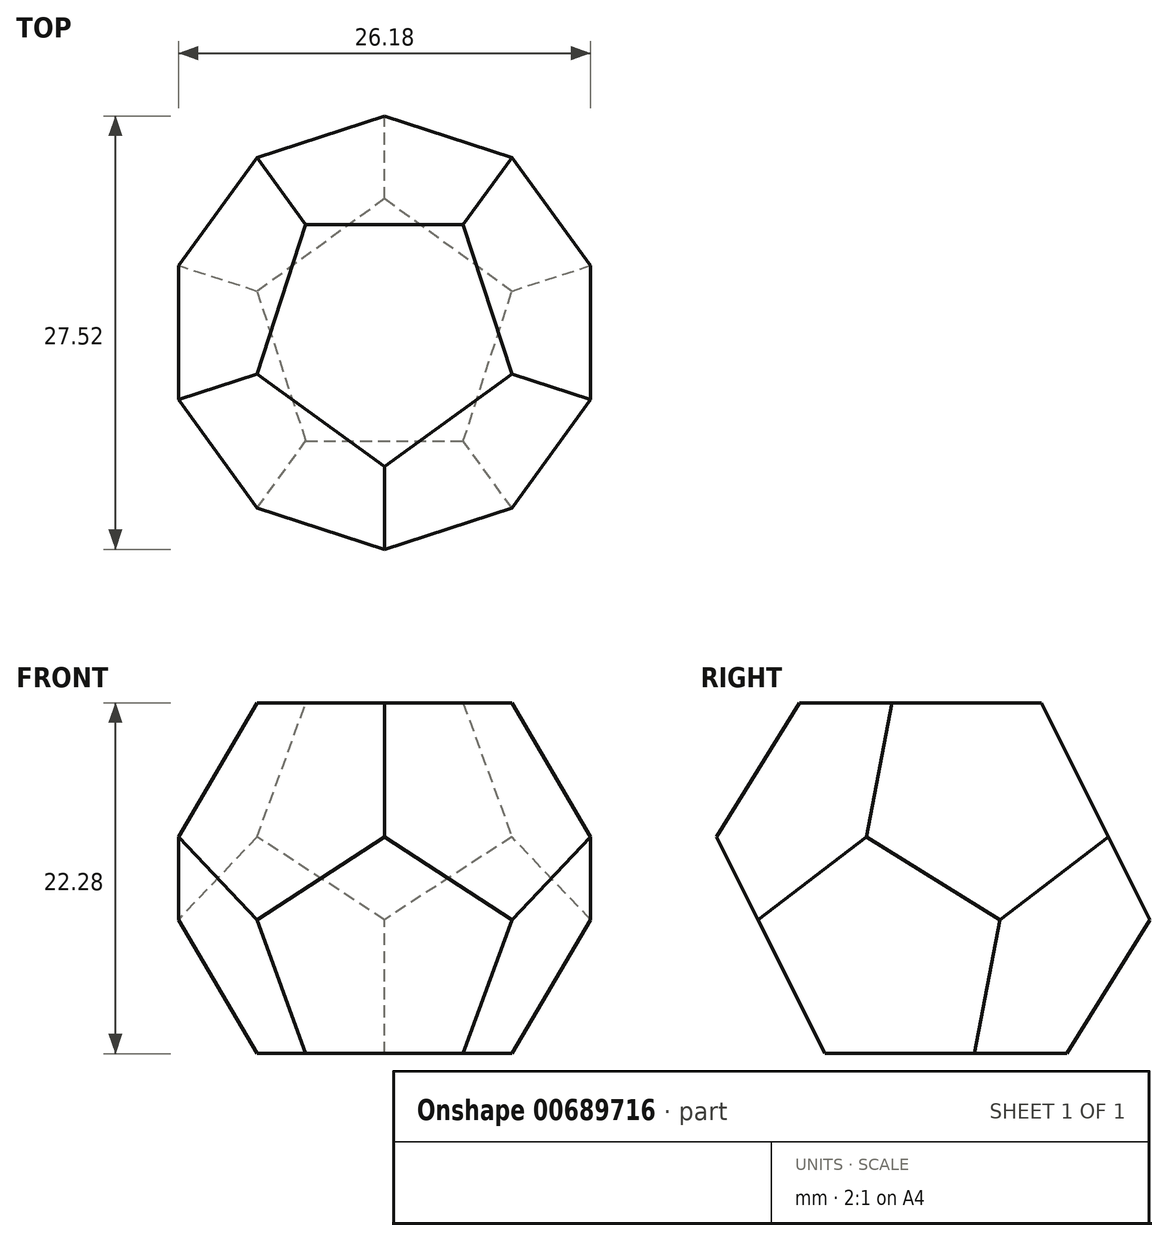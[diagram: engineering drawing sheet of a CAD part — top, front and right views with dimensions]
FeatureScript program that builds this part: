
annotation { "Feature Type Name" : "Feature", "Feature Type Description" : "" }
export const myFeature = defineFeature(function(context is Context, id is Id, definition is map)
    precondition{}
    {
        {
            var Q0;
            Q0=qCreatedBy(makeId("Top.planeOp"),FACE);
            var sketch = newSketch(context, id + "F0", { "sketchPlane" : qUnion([Q0])});
            skCircle(sketch, "E0.cCircle", {"center": v(0, 0) * mm, "radius": 6.88 * mm, "construction": true});
            skLineSegment(sketch, "E0.0", {"start": v(-5, 6.88) * mm, "end": v(5, 6.88) * mm});
            skLineSegment(sketch, "E0.1", {"start": v(5, 6.88) * mm, "end": v(8.1, -2.63) * mm});
            skLineSegment(sketch, "E0.2", {"start": v(8.1, -2.63) * mm, "end": v(0, -8.5) * mm});
            skLineSegment(sketch, "E0.3", {"start": v(0, -8.5) * mm, "end": v(-8.1, -2.63) * mm});
            skLineSegment(sketch, "E0.4", {"start": v(-8.1, -2.63) * mm, "end": v(-5, 6.88) * mm});
            skPoint(sketch, "E0.0.midPoint", {"position": v(0, 6.88) * mm});
            skLineSegment(sketch, "E1", {"start": v(8.1, -2.63) * mm, "end": v(13.1, -4.25) * mm});
            skLineSegment(sketch, "E2", {"start": v(0, -8.5) * mm, "end": v(0, -13.76) * mm});
            skLineSegment(sketch, "E3", {"start": v(-8.1, -2.63) * mm, "end": v(-13.1, -4.25) * mm});
            skLineSegment(sketch, "E4", {"start": v(-5, 6.88) * mm, "end": v(-8.1, 11.14) * mm});
            skLineSegment(sketch, "E5", {"start": v(5, 6.88) * mm, "end": v(8.1, 11.14) * mm});
            skLineSegment(sketch, "E6", {"start": v(0, -13.76) * mm, "end": v(-8.1, -11.14) * mm});
            skLineSegment(sketch, "E7", {"start": v(-8.1, -11.14) * mm, "end": v(-13.1, -4.25) * mm});
            skLineSegment(sketch, "E8", {"start": v(-13.1, -4.25) * mm, "end": v(-13.1, 4.25) * mm});
            skLineSegment(sketch, "E9", {"start": v(-13.1, 4.25) * mm, "end": v(-8.1, 11.14) * mm});
            skLineSegment(sketch, "E10", {"start": v(-8.1, 11.14) * mm, "end": v(0, 13.76) * mm});
            skLineSegment(sketch, "E11", {"start": v(0, 13.76) * mm, "end": v(8.1, 11.14) * mm});
            skLineSegment(sketch, "E12", {"start": v(8.1, 11.14) * mm, "end": v(13.1, 4.25) * mm});
            skLineSegment(sketch, "E13", {"start": v(13.1, -4.25) * mm, "end": v(13.1, 4.25) * mm});
            skLineSegment(sketch, "E14", {"start": v(0, -13.76) * mm, "end": v(8.1, -11.14) * mm});
            skLineSegment(sketch, "E15", {"start": v(13.1, -4.25) * mm, "end": v(8.1, -11.14) * mm});
            skSolve(sketch);
        }
        {
            var Q0;
            Q0=qCreatedBy(makeId("Right.planeOp"),FACE);
            var sketch = newSketch(context, id + "F1", { "sketchPlane" : qUnion([Q0])});
            skLineSegment(sketch, "E16", {"start": v(6.88, 11.14) * mm, "end": v(-8.5, 11.14) * mm});
            skLineSegment(sketch, "E17", {"start": v(6.88, 11.14) * mm, "end": v(13.76, -2.63) * mm});
            skLineSegment(sketch, "E18", {"start": v(-8.5, 11.14) * mm, "end": v(-13.76, 2.63) * mm});
            skLineSegment(sketch, "E19", {"start": v(-6.88, -11.14) * mm, "end": v(8.5, -11.14) * mm});
            skLineSegment(sketch, "E20", {"start": v(0, 0) * mm, "end": v(0, 11.14) * mm, "construction": true});
            skLineSegment(sketch, "E21", {"start": v(0, 0) * mm, "end": v(0, -11.14) * mm});
            skLineSegment(sketch, "E22", {"start": v(-6.88, -11.14) * mm, "end": v(-13.76, 2.63) * mm});
            skLineSegment(sketch, "E23", {"start": v(8.5, -11.14) * mm, "end": v(13.76, -2.63) * mm});
            skLineSegment(sketch, "E24", {"start": v(-10.32, -4.25) * mm, "end": v(10.32, 4.25) * mm, "construction": true});
            skLineSegment(sketch, "E25", {"start": v(-2.63, 11.14) * mm, "end": v(-4.25, 2.63) * mm});
            skLineSegment(sketch, "E26", {"start": v(-4.25, 2.63) * mm, "end": v(-11.14, -2.63) * mm});
            skLineSegment(sketch, "E27", {"start": v(-4.25, 2.63) * mm, "end": v(4.25, -2.63) * mm});
            skLineSegment(sketch, "E28", {"start": v(4.25, -2.63) * mm, "end": v(2.63, -11.14) * mm});
            skLineSegment(sketch, "E29", {"start": v(4.25, -2.63) * mm, "end": v(11.14, 2.63) * mm});
            skCircle(sketch, "E30", {"center": v(0, 0) * mm, "radius": 14.01 * mm, "construction": true});
            skSolve(sketch);
        }
        {
            var Q0;
            Q0=sQuery(id+"F1.wireOp",VERTEX,"E20.end");
            var Q1;
            Q1=sQuery(id+"F1.wireOp",EDGE,"E20");
            cPlane(context, id + "F2", {"entities" : qUnion([Q0, Q1]), "cplaneType" : CPlaneType.LINE_POINT, "offset" : 25 * mm, "width" : 150 * mm, "height" : 150 * mm});
        }
        {
            var Q0;
            Q0=qCreatedBy(id+"F2.planeOp",FACE);
            var sketch = newSketch(context, id + "F3", { "sketchPlane" : qUnion([Q0])});
            skLineSegment(sketch, "E31.0", {"start": v(-5, 6.88) * mm, "end": v(5, 6.88) * mm});
            skLineSegment(sketch, "E31.1", {"start": v(-8.1, -2.63) * mm, "end": v(-5, 6.88) * mm});
            skLineSegment(sketch, "E31.2", {"start": v(0, -8.5) * mm, "end": v(-8.1, -2.63) * mm});
            skLineSegment(sketch, "E31.3", {"start": v(8.1, -2.63) * mm, "end": v(0, -8.5) * mm});
            skLineSegment(sketch, "E31.4", {"start": v(5, 6.88) * mm, "end": v(8.1, -2.63) * mm});
            skSolve(sketch);
        }
        {
            var Q0;
            Q0 = qSketchRegion(id + "F3", true);
            var Q1;
            Q1=sQuery(id+"F0.wireOp",VERTEX,"E0.cCircle.center");
            loft(context, id + "F4", {"sheetProfilesArray" : [{ "sheetProfileEntities" : qUnion([Q0]) }, { "sheetProfileEntities" : qUnion([Q1]) }]});
        }
        {
            var Q0;
            Q0=makeQuery(id+"F4.opLoft","SWEPT_BODY",BODY,{"disambiguationData":[OSD([sQuery(id+"F0.wireOp",VERTEX,"E0.cCircle.center"),makeQuery(id+"F3.imprint","IMPRINT",FACE,{"disambiguationData":[TD([[makeQuery(id+"F3.imprint","IMPRINT",EDGE,{"derivedFrom":sQuery(id+"F3.wireOp",EDGE,"E31.0")}),-1.0]])]})])]});
            var Q1;
            Q1=makeQuery(id+"F4.opLoft","SWEPT_FACE",FACE,{"disambiguationData":[OSD([sQuery(id+"F3.wireOp",EDGE,"E31.0"),sQuery(id+"F3.wireOp",EDGE,"E31.1"),sQuery(id+"F3.wireOp",EDGE,"E31.4")])]});
            mirror(context, id + "F5", {"entities" : qUnion([Q0]), "mirrorPlane" : qUnion([Q1])});
        }
        {
            var Q0;
            Q0=makeQuery(id+"F5.opPattern","COPY",BODY,{"derivedFrom":makeQuery(id+"F4.opLoft","SWEPT_BODY",BODY,{"disambiguationData":[OSD([sQuery(id+"F0.wireOp",VERTEX,"E0.cCircle.center"),makeQuery(id+"F3.imprint","IMPRINT",FACE,{"disambiguationData":[TD([[makeQuery(id+"F3.imprint","IMPRINT",EDGE,{"derivedFrom":sQuery(id+"F3.wireOp",EDGE,"E31.0")}),-1.0]])]})])]}),"instanceName":"1"});
            var Q1;
            Q1=sQuery(id+"F1.wireOp",EDGE,"E20");
            circularPattern(context, id + "F6", {"entities" : qUnion([Q0]), "axis" : qUnion([Q1]), "angle" : 360 * degree, "instanceCount" : 5, "equalSpace" : true});
        }
        {
            var Q0;
            Q0=makeQuery(id+"F4.opLoft","SWEPT_BODY",BODY,{"disambiguationData":[OSD([sQuery(id+"F0.wireOp",VERTEX,"E0.cCircle.center"),makeQuery(id+"F3.imprint","IMPRINT",FACE,{"disambiguationData":[TD([[makeQuery(id+"F3.imprint","IMPRINT",EDGE,{"derivedFrom":sQuery(id+"F3.wireOp",EDGE,"E31.0")}),-1.0]])]})])]});
            var Q1;
            Q1=makeQuery(id+"F6.opPattern","COPY",BODY,{"derivedFrom":makeQuery(id+"F5.opPattern","COPY",BODY,{"derivedFrom":makeQuery(id+"F4.opLoft","SWEPT_BODY",BODY,{"disambiguationData":[OSD([sQuery(id+"F0.wireOp",VERTEX,"E0.cCircle.center"),makeQuery(id+"F3.imprint","IMPRINT",FACE,{"disambiguationData":[TD([[makeQuery(id+"F3.imprint","IMPRINT",EDGE,{"derivedFrom":sQuery(id+"F3.wireOp",EDGE,"E31.0")}),-1.0]])]})])]}),"instanceName":"1"}),"instanceName":"3"});
            var Q2;
            Q2=makeQuery(id+"F6.opPattern","COPY",BODY,{"derivedFrom":makeQuery(id+"F5.opPattern","COPY",BODY,{"derivedFrom":makeQuery(id+"F4.opLoft","SWEPT_BODY",BODY,{"disambiguationData":[OSD([sQuery(id+"F0.wireOp",VERTEX,"E0.cCircle.center"),makeQuery(id+"F3.imprint","IMPRINT",FACE,{"disambiguationData":[TD([[makeQuery(id+"F3.imprint","IMPRINT",EDGE,{"derivedFrom":sQuery(id+"F3.wireOp",EDGE,"E31.0")}),-1.0]])]})])]}),"instanceName":"1"}),"instanceName":"4"});
            var Q3;
            Q3=makeQuery(id+"F5.opPattern","COPY",BODY,{"derivedFrom":makeQuery(id+"F4.opLoft","SWEPT_BODY",BODY,{"disambiguationData":[OSD([sQuery(id+"F0.wireOp",VERTEX,"E0.cCircle.center"),makeQuery(id+"F3.imprint","IMPRINT",FACE,{"disambiguationData":[TD([[makeQuery(id+"F3.imprint","IMPRINT",EDGE,{"derivedFrom":sQuery(id+"F3.wireOp",EDGE,"E31.0")}),-1.0]])]})])]}),"instanceName":"1"});
            var Q4;
            Q4=makeQuery(id+"F6.opPattern","COPY",BODY,{"derivedFrom":makeQuery(id+"F5.opPattern","COPY",BODY,{"derivedFrom":makeQuery(id+"F4.opLoft","SWEPT_BODY",BODY,{"disambiguationData":[OSD([sQuery(id+"F0.wireOp",VERTEX,"E0.cCircle.center"),makeQuery(id+"F3.imprint","IMPRINT",FACE,{"disambiguationData":[TD([[makeQuery(id+"F3.imprint","IMPRINT",EDGE,{"derivedFrom":sQuery(id+"F3.wireOp",EDGE,"E31.0")}),-1.0]])]})])]}),"instanceName":"1"}),"instanceName":"2"});
            var Q5;
            Q5=makeQuery(id+"F6.opPattern","COPY",BODY,{"derivedFrom":makeQuery(id+"F5.opPattern","COPY",BODY,{"derivedFrom":makeQuery(id+"F4.opLoft","SWEPT_BODY",BODY,{"disambiguationData":[OSD([sQuery(id+"F0.wireOp",VERTEX,"E0.cCircle.center"),makeQuery(id+"F3.imprint","IMPRINT",FACE,{"disambiguationData":[TD([[makeQuery(id+"F3.imprint","IMPRINT",EDGE,{"derivedFrom":sQuery(id+"F3.wireOp",EDGE,"E31.0")}),-1.0]])]})])]}),"instanceName":"1"}),"instanceName":"1"});
            var Q6;
            Q6=sQuery(id+"F1.wireOp",EDGE,"E30");
            circularPattern(context, id + "F7", {"operationType" : NewBodyOperationType.ADD, "entities" : qUnion([Q0, Q1, Q2, Q3, Q4, Q5]), "axis" : qUnion([Q6]), "angle" : 360 * degree, "instanceCount" : 2, "equalSpace" : true});
        }
    });
